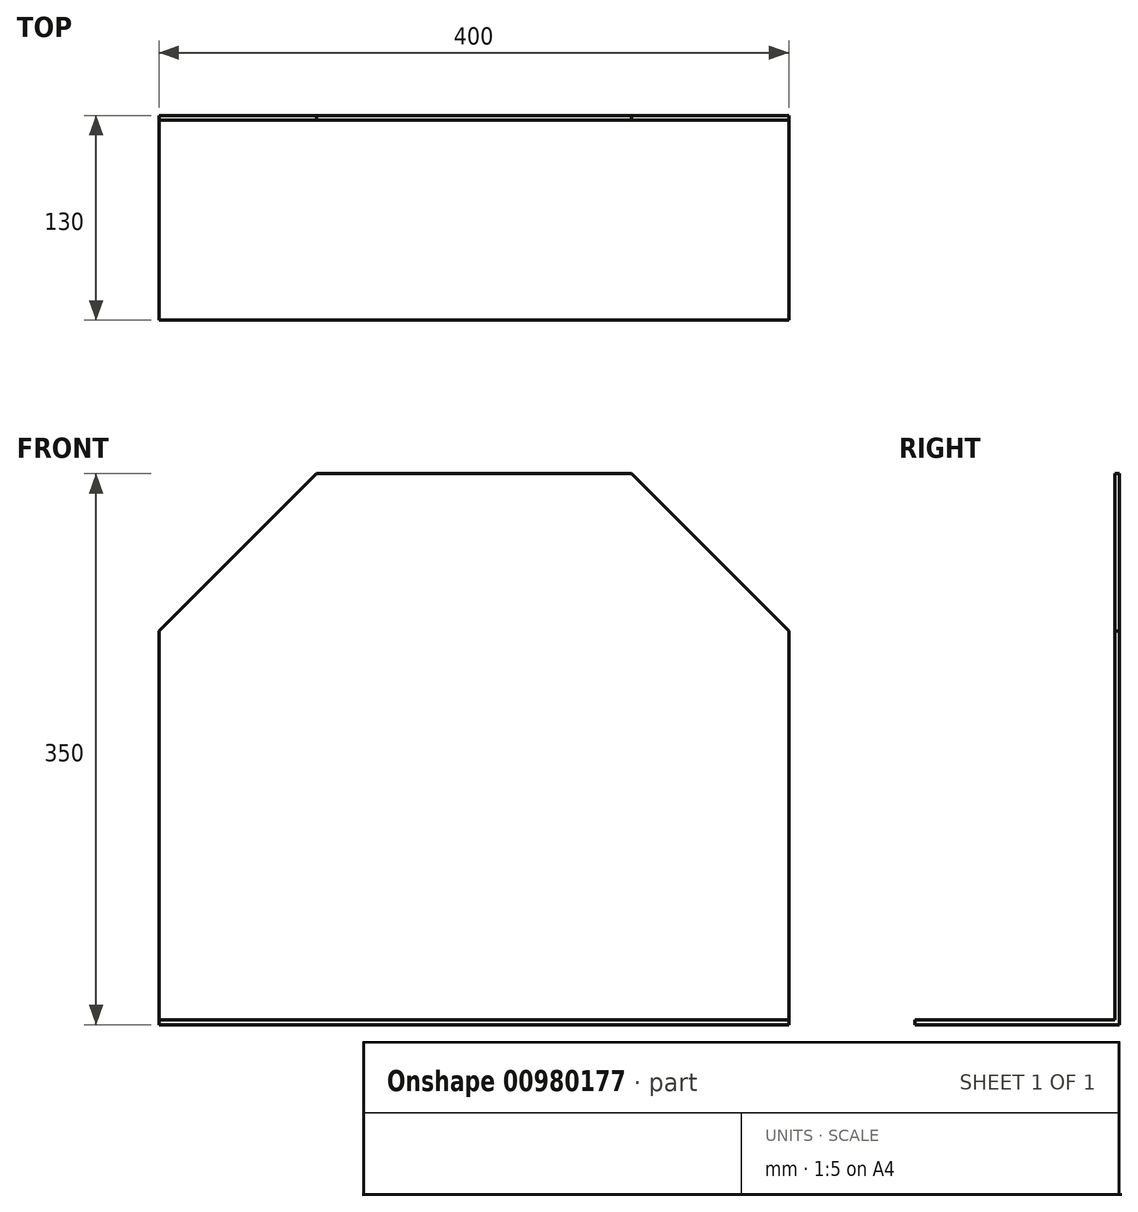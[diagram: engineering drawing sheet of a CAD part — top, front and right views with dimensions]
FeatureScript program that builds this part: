
annotation { "Feature Type Name" : "Feature", "Feature Type Description" : "" }
export const myFeature = defineFeature(function(context is Context, id is Id, definition is map)
    precondition{}
    {
        {
            var Q0;
            Q0=qCreatedBy(makeId("Right.planeOp"),FACE);
            var sketch = newSketch(context, id + "F0", { "sketchPlane" : qUnion([Q0])});
            skLineSegment(sketch, "E0", {"start": v(0, 0) * mm, "end": v(0, 350) * mm});
            skLineSegment(sketch, "E1", {"start": v(0, 350) * mm, "end": v(-3, 350) * mm});
            skLineSegment(sketch, "E2", {"start": v(-3, 350) * mm, "end": v(-3, 3) * mm});
            skLineSegment(sketch, "E3", {"start": v(-3, 3) * mm, "end": v(-130, 3) * mm});
            skLineSegment(sketch, "E4", {"start": v(-130, 3) * mm, "end": v(-130, 0) * mm});
            skLineSegment(sketch, "E5", {"start": v(-130, 0) * mm, "end": v(0, 0) * mm});
            skSolve(sketch);
        }
        {
            var Q0;
            Q0 = qSketchRegion(id + "F0", true);
            extrude(context, id + "F1", {"entities" : qUnion([Q0]), "endBound" : BoundingType.SYMMETRIC, "depth" : 400 * mm, "offsetDistance" : 25 * mm});
        }
        {
            var Q0;
            Q0=makeQuery(id+"F1.opExtrude","CAP_EDGE",EDGE,{"disambiguationData":[OSD([sQuery(id+"F0.wireOp",EDGE,"E1")])],"isStart":false});
            var Q1;
            Q1=makeQuery(id+"F1.opExtrude","CAP_EDGE",EDGE,{"disambiguationData":[OSD([sQuery(id+"F0.wireOp",EDGE,"E1")])],"isStart":true});
            chamfer(context, id + "F2", {"entities" : qUnion([Q0, Q1]), "width" : 100 * mm, "tangentPropagation" : true});
        }
    });
